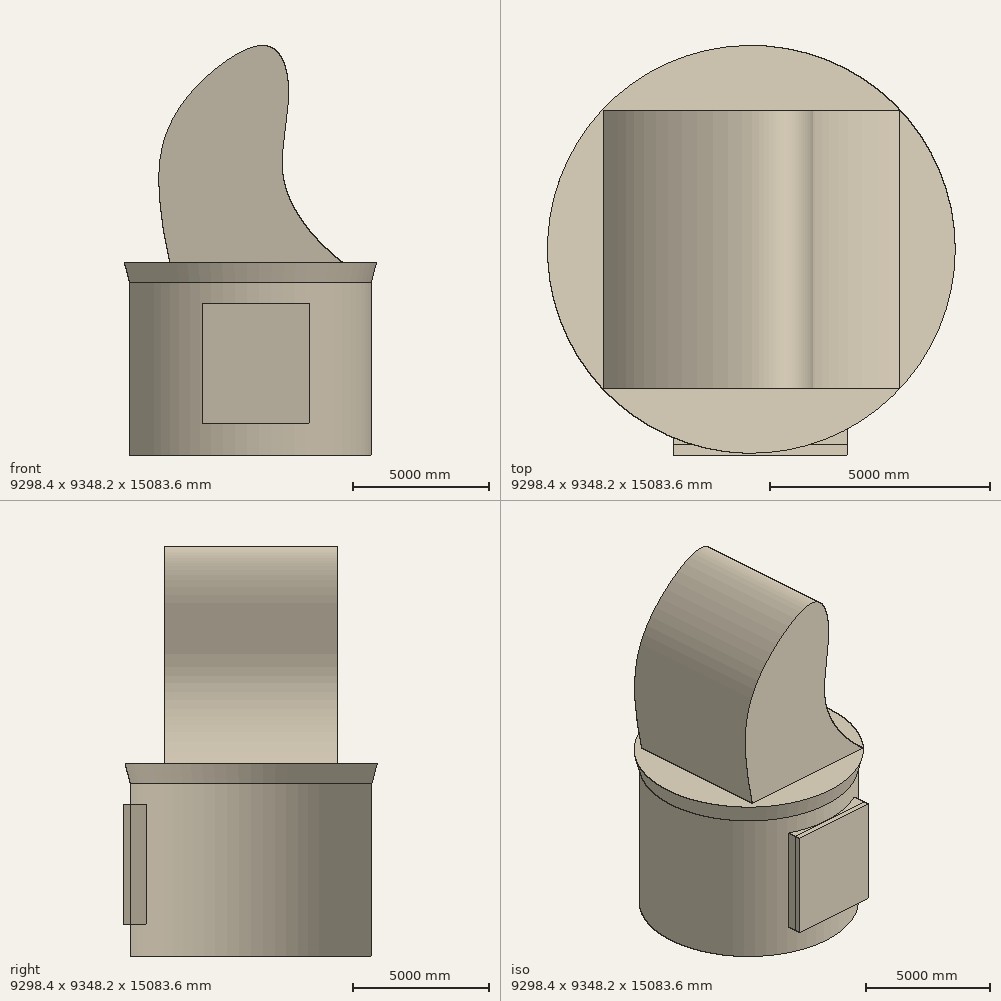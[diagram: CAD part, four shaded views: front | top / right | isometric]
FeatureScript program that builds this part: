
annotation { "Feature Type Name" : "Feature", "Feature Type Description" : "" }
export const myFeature = defineFeature(function(context is Context, id is Id, definition is map)
    precondition{}
    {
        {
            var Q0;
            Q0=qCreatedBy(makeId("Top.planeOp"),FACE);
            var sketch = newSketch(context, id + "F0", { "sketchPlane" : qUnion([Q0])});
            skCircle(sketch, "E0", {"center": v(0, 0) * mm, "radius": 4445 * mm});
            skSolve(sketch);
        }
        {
            var Q0;
            Q0 = qSketchRegion(id + "F0", true);
            extrude(context, id + "F1", {"entities" : qUnion([Q0]), "depth" : 6350 * mm, "offsetDistance" : 25.4 * mm});
        }
        {
            var Q0;
            Q0=makeQuery(id+"F1.opExtrude","CAP_FACE",FACE,{"disambiguationData":[OSD([sQuery(id+"F0.wireOp",EDGE,"E0")])],"isStart":false});
            var sketch = newSketch(context, id + "F2", { "sketchPlane" : qUnion([Q0])});
            skCircle(sketch, "E1", {"center": v(0, 0) * mm, "radius": 4919.8 * mm});
            skSolve(sketch);
        }
        {
            var Q0;
            Q0=makeQuery(id+"F2.imprint","IMPRINT",FACE,{"disambiguationData":[TD([[makeQuery(id+"F2.imprint","IMPRINT",EDGE,{"derivedFrom":makeQuery(id+"F1.opExtrude","CAP_EDGE",EDGE,{"disambiguationData":[OSD([sQuery(id+"F0.wireOp",EDGE,"E0")])],"isStart":false})}),1.0]])]});
            extrude(context, id + "F3", {"entities" : qUnion([Q0]), "depth" : 762 * mm, "offsetDistance" : 25.4 * mm, "hasDraft" : true, "draftAngle" : 15 * degree});
        }
        {
            var Q0;
            Q0=makeQuery(id+"F1.opExtrude","CAP_FACE",FACE,{"disambiguationData":[OSD([sQuery(id+"F0.wireOp",EDGE,"E0")])],"isStart":true});
            var sketch = newSketch(context, id + "F4", { "sketchPlane" : qUnion([Q0])});
            skLineSegment(sketch, "E2", {"start": v(0, 4445) * mm, "end": v(-5191.35, 4445) * mm});
            skSolve(sketch);
        }
        {
            var Q0;
            Q0=sQuery(id+"F4.wireOp",EDGE,"E2");
            var Q1;
            Q1=makeQuery(id+"F1.opExtrude","SWEPT_FACE",FACE,{"disambiguationData":[OSD([sQuery(id+"F0.wireOp",EDGE,"E0")])]});
            cPlane(context, id + "F5", {"entities" : qUnion([Q0, Q1]), "cplaneType" : CPlaneType.LINE_ANGLE, "offset" : 25.4 * mm, "angle" : 0 * degree, "width" : 152.4 * mm, "height" : 152.4 * mm});
        }
        {
            var Q0;
            Q0=qCreatedBy(id+"F5.planeOp",FACE);
            var sketch = newSketch(context, id + "F6", { "sketchPlane" : qUnion([Q0])});
            skLineSegment(sketch, "E3.bottom", {"start": v(-1772.55, 5599.66) * mm, "end": v(2182.55, 5599.66) * mm});
            skLineSegment(sketch, "E3.top", {"start": v(-1772.55, 1186.25) * mm, "end": v(2182.55, 1186.25) * mm});
            skLineSegment(sketch, "E3.left", {"start": v(-1772.55, 5599.66) * mm, "end": v(-1772.55, 1186.25) * mm});
            skLineSegment(sketch, "E3.right", {"start": v(2182.55, 5599.66) * mm, "end": v(2182.55, 1186.25) * mm});
            skSolve(sketch);
        }
        {
            var Q0;
            Q0=makeQuery(id+"F6.imprint","IMPRINT",FACE,{"disambiguationData":[TD([[makeQuery(id+"F6.imprint","IMPRINT",EDGE,{"derivedFrom":sQuery(id+"F6.wireOp",EDGE,"E3.bottom")}),-1.0]])]});
            extrude(context, id + "F7", {"entities" : qUnion([Q0]), "oppositeDirection" : true, "depth" : 762 * mm, "offsetDistance" : 25.4 * mm});
        }
        {
            var Q0;
            Q0=makeQuery(id+"F7.opExtrude","CAP_FACE",FACE,{"disambiguationData":[OSD([sQuery(id+"F6.wireOp",EDGE,"E3.bottom"),sQuery(id+"F6.wireOp",EDGE,"E3.top"),sQuery(id+"F6.wireOp",EDGE,"E3.left"),sQuery(id+"F6.wireOp",EDGE,"E3.right")])],"isStart":true});
            extrude(context, id + "F8", {"entities" : qUnion([Q0]), "depth" : 254 * mm, "offsetDistance" : 25.4 * mm});
        }
        {
            var Q0;
            Q0=qCreatedBy(id+"F5.planeOp",FACE);
            var sketch = newSketch(context, id + "F9", { "sketchPlane" : qUnion([Q0])});
            skLineSegment(sketch, "E4", {"start": v(-2970, 7112) * mm, "end": v(3380, 7112) * mm});
            skFitSpline(sketch, "E5", {"points": [v(-2970, 7112) * mm, v(-3315.55, 10960.2) * mm, v(-1786.1, 13758.52) * mm, v(695, 15050.05) * mm, v(1408.73, 13282.7) * mm, v(1238.8, 10087.85) * mm, v(3380, 7112) * mm], "startDerivative": vector(-4200.88, 18927.98) * mm, "endDerivative": vector(16080.23, -12407.22) * mm});
            skSolve(sketch);
        }
        {
            var Q0;
            Q0 = qSketchRegion(id + "F9", true);
            extrude(context, id + "F10", {"entities" : qUnion([Q0]), "oppositeDirection" : true, "depth" : 7620 * mm, "offsetDistance" : 25.4 * mm, "hasSecondDirection" : true, "secondDirectionOppositeDirection" : true, "secondDirectionDepth" : 1270 * mm});
        }
    });
